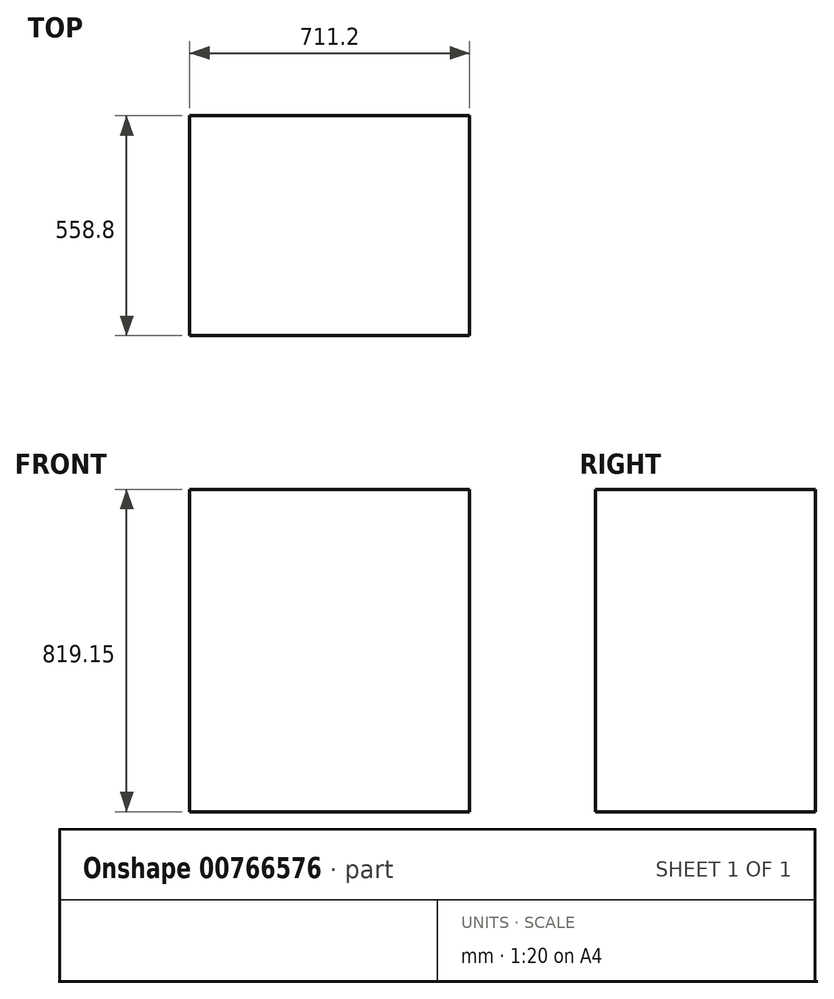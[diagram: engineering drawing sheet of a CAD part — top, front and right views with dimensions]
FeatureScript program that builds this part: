
annotation { "Feature Type Name" : "Feature", "Feature Type Description" : "" }
export const myFeature = defineFeature(function(context is Context, id is Id, definition is map)
    precondition{}
    {
        {
            var Q0;
            Q0=qCreatedBy(makeId("Top.planeOp"),FACE);
            var sketch = newSketch(context, id + "F0", { "sketchPlane" : qUnion([Q0])});
            skLineSegment(sketch, "E0.bottom", {"start": v(-355.6, 279.4) * mm, "end": v(355.6, 279.4) * mm});
            skLineSegment(sketch, "E0.top", {"start": v(-355.6, -279.4) * mm, "end": v(355.6, -279.4) * mm});
            skLineSegment(sketch, "E0.left", {"start": v(-355.6, 279.4) * mm, "end": v(-355.6, -279.4) * mm});
            skLineSegment(sketch, "E0.right", {"start": v(355.6, 279.4) * mm, "end": v(355.6, -279.4) * mm});
            skLineSegment(sketch, "E1", {"start": v(-355.6, 279.4) * mm, "end": v(355.6, -279.4) * mm});
            skSolve(sketch);
        }
        {
            var Q0;
            Q0 = qSketchRegion(id + "F0", true);
            extrude(context, id + "F1", {"entities" : qUnion([Q0]), "depth" : 819.15 * mm, "offsetDistance" : 25.4 * mm});
        }
    });
